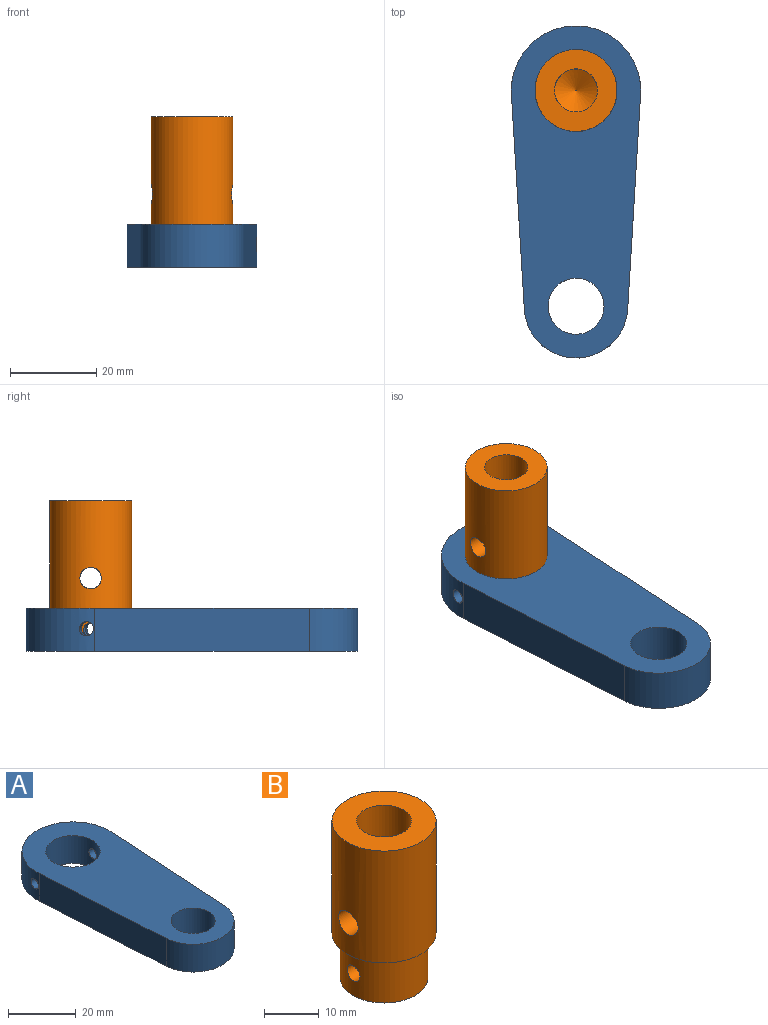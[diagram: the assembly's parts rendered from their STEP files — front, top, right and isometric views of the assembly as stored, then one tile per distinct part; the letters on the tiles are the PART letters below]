
ASSEMBLY  parts=2 mates=1
PART A: 10 faces, bbox 30.1x77x10 mm
  f0: cylinder r=8mm len=16mm, axis (0,0,-1), area 485.5mm2, adj f6,f7,f8,f9
  f1: cylinder r=15mm len=30mm, axis (0,0,-1), area 476.1mm2, adj f2,f4,f6,f7,f8,f9
  f2: plane 49.82x10mm, normal (-1,-0.06,0), area 499.1mm2, adj f1,f3,f6,f7
  f3: cylinder r=12mm len=23.96mm, axis (0,0,-1), area 362.6mm2, adj f2,f4,f6,f7
  f4: plane 49.82x10mm, normal (1,-0.06,0), area 495.1mm2, adj f1,f3,f6,f7,f9
  f5: cylinder r=6.5mm len=13mm, axis (0,0,-1), area 408.4mm2, adj f6,f7
  f6: plane 77x30mm, normal (0,0,1), area 1598.3mm2, adj f0,f1,f2,f3,f4,f5
  f7: plane 77x30mm, normal (0,0,-1), area 1598.3mm2, adj f0,f1,f2,f3,f4,f5
  f8: cylinder r=1.65mm len=7.38mm, axis (1,-0.06,0), area 73mm2, adj f0,f1
  f9: cylinder r=1.65mm len=7.38mm, axis (1,-0.06,0), area 73.2mm2, adj f0,f1,f4
PART B: 12 faces, bbox 19x19x35 mm
  f0: cylinder r=9.5mm len=25mm, axis (0,0,-1), area 1452.6mm2, adj f5,f6,f9,f11
  f1: cylinder r=5mm len=22mm, axis (0,0,1), area 650.5mm2, adj f5,f7,f9,f11
  f2: cylinder r=0.01mm len=3.35mm, axis (0,0,1), area 0.2mm2, adj f8,f10
  f3: cylinder r=0.01mm len=3.35mm, axis (0,0,1), area 0.2mm2, adj f7,f10
  f4: cylinder r=8mm len=16mm, axis (0,0,1), area 485.4mm2, adj f6,f8,f10
  f5: plane 19x19mm, normal (0,0,1), area 205mm2, adj f0,f1
  f6: plane 19x19mm, normal (0,0,-1), area 82.5mm2, adj f0,f4
  f7: cone r=0mm half-angle=59deg, axis (0,0,1), area 91.6mm2, adj f1,f3
  f8: plane 16x16mm, normal (0,0,-1), area 201.1mm2, adj f2,f4
  f9: cylinder r=2.5mm len=5.17mm, axis (-1,0,0), area 73.2mm2, adj f0,f1
  f10: cylinder r=1.65mm len=16mm, axis (-1,0,0), area 164.1mm2, adj f2,f3,f4
  f11: cylinder r=2.5mm len=5.17mm, axis (1,0,0), area 73.2mm2, adj f0,f1
PLACE A rot(axis=(-0.85,-0.02,-0.52),0deg) t=(28.65,2.13,-51.69)mm
PLACE B rot(axis=(0,0,1),180deg) t=(76.92,2.13,-41.69)mm
MATE revolute B.f0 <-> A.f0  axis (0,0,-1) through (76.92,2.13,-51.69)mm
